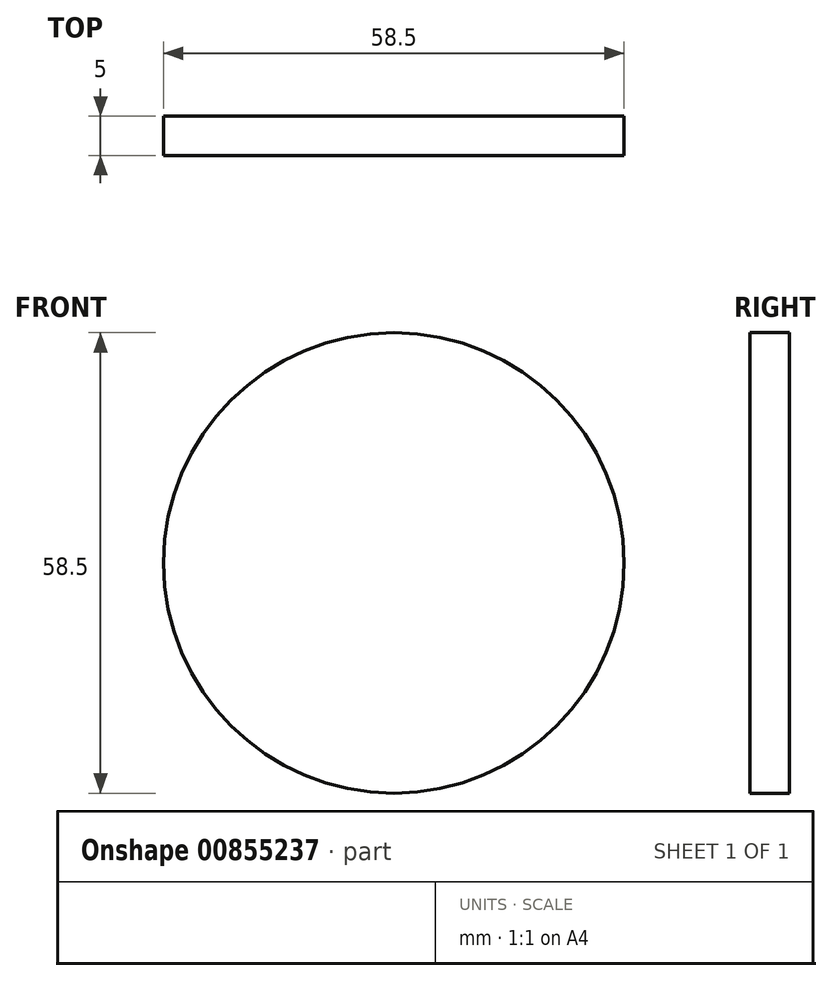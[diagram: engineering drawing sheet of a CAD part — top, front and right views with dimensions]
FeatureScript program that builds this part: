
annotation { "Feature Type Name" : "Feature", "Feature Type Description" : "" }
export const myFeature = defineFeature(function(context is Context, id is Id, definition is map)
    precondition{}
    {
        {
            var Q0;
            Q0=qCreatedBy(makeId("Front.planeOp"),FACE);
            var sketch = newSketch(context, id + "F0", { "sketchPlane" : qUnion([Q0])});
            skCircle(sketch, "E0", {"center": v(-35.75, -156.4) * mm, "radius": 29.25 * mm});
            skCircle(sketch, "E1", {"center": v(-40.8, 87.55) * mm, "radius": 24.8 * mm});
            skCircle(sketch, "E2", {"center": v(-40.8, 30.05) * mm, "radius": 24.8 * mm});
            skCircle(sketch, "E3", {"center": v(-40.8, -27.45) * mm, "radius": 24.8 * mm});
            skCircle(sketch, "E4", {"center": v(-35.75, -91.4) * mm, "radius": 29.25 * mm});
            skCircle(sketch, "E5", {"center": v(110.8, -147.35) * mm, "radius": 24.8 * mm});
            skCircle(sketch, "E6", {"center": v(110.8, -81.75) * mm, "radius": 24.8 * mm});
            skCircle(sketch, "E7", {"center": v(110.8, -16.15) * mm, "radius": 24.8 * mm});
            skCircle(sketch, "E8", {"center": v(-100.4, 87.55) * mm, "radius": 24.8 * mm});
            skCircle(sketch, "E9", {"center": v(-100.4, 30.05) * mm, "radius": 24.8 * mm});
            skCircle(sketch, "E10", {"center": v(-100.4, -27.45) * mm, "radius": 24.8 * mm});
            skCircle(sketch, "E11", {"center": v(-111.3, -91.4) * mm, "radius": 19.3 * mm});
            skCircle(sketch, "E12", {"center": v(-111.3, -145) * mm, "radius": 19.3 * mm});
            skCircle(sketch, "E13", {"center": v(-348.3, -27.45) * mm, "radius": 39.95 * mm});
            skCircle(sketch, "E14", {"center": v(-122.85, 110) * mm, "radius": 2.3 * mm});
            skCircle(sketch, "E15", {"center": v(-77.95, 65.1) * mm, "radius": 2.6 * mm});
            skArc(sketch, "E16", {"start": v(-115.72, 111.7) * mm, "mid": v(-113.34, 111.02) * mm, "end": v(-112.66, 113.4) * mm});
            skLineSegment(sketch, "E17", {"start": v(-112.66, 113.4) * mm, "end": v(-114.34, 116.45) * mm});
            skArc(sketch, "E18", {"start": v(-114.34, 116.45) * mm, "mid": v(-116.72, 117.15) * mm, "end": v(-117.41, 114.77) * mm});
            skLineSegment(sketch, "E19", {"start": v(-117.41, 114.77) * mm, "end": v(-115.72, 111.7) * mm});
            skCircle(sketch, "E20", {"center": v(-122.85, 110) * mm, "radius": 3.95 * mm});
            skCircle(sketch, "E21", {"center": v(-63.25, 110) * mm, "radius": 2.3 * mm});
            skCircle(sketch, "E22", {"center": v(-18.35, 65.1) * mm, "radius": 2.6 * mm});
            skArc(sketch, "E23", {"start": v(-56.12, 111.7) * mm, "mid": v(-53.74, 111.02) * mm, "end": v(-53.06, 113.4) * mm});
            skLineSegment(sketch, "E24", {"start": v(-53.06, 113.4) * mm, "end": v(-54.74, 116.45) * mm});
            skArc(sketch, "E25", {"start": v(-54.74, 116.45) * mm, "mid": v(-57.12, 117.15) * mm, "end": v(-57.81, 114.77) * mm});
            skLineSegment(sketch, "E26", {"start": v(-57.81, 114.77) * mm, "end": v(-56.12, 111.7) * mm});
            skCircle(sketch, "E27", {"center": v(-63.25, 110) * mm, "radius": 3.95 * mm});
            skCircle(sketch, "E28", {"center": v(-122.85, 52.5) * mm, "radius": 2.3 * mm});
            skCircle(sketch, "E29", {"center": v(-77.95, 7.6) * mm, "radius": 2.6 * mm});
            skArc(sketch, "E30", {"start": v(-115.72, 54.2) * mm, "mid": v(-113.34, 53.52) * mm, "end": v(-112.66, 55.9) * mm});
            skLineSegment(sketch, "E31", {"start": v(-112.66, 55.9) * mm, "end": v(-114.34, 58.95) * mm});
            skArc(sketch, "E32", {"start": v(-114.34, 58.95) * mm, "mid": v(-116.72, 59.65) * mm, "end": v(-117.41, 57.27) * mm});
            skLineSegment(sketch, "E33", {"start": v(-117.41, 57.27) * mm, "end": v(-115.72, 54.2) * mm});
            skCircle(sketch, "E34", {"center": v(-122.85, 52.5) * mm, "radius": 3.95 * mm});
            skCircle(sketch, "E35", {"center": v(-63.25, 52.5) * mm, "radius": 2.3 * mm});
            skCircle(sketch, "E36", {"center": v(-18.35, 7.6) * mm, "radius": 2.6 * mm});
            skArc(sketch, "E37", {"start": v(-56.12, 54.2) * mm, "mid": v(-53.74, 53.52) * mm, "end": v(-53.06, 55.9) * mm});
            skLineSegment(sketch, "E38", {"start": v(-53.06, 55.9) * mm, "end": v(-54.74, 58.95) * mm});
            skArc(sketch, "E39", {"start": v(-54.74, 58.95) * mm, "mid": v(-57.12, 59.65) * mm, "end": v(-57.81, 57.27) * mm});
            skLineSegment(sketch, "E40", {"start": v(-57.81, 57.27) * mm, "end": v(-56.12, 54.2) * mm});
            skCircle(sketch, "E41", {"center": v(-63.25, 52.5) * mm, "radius": 3.95 * mm});
            skCircle(sketch, "E42", {"center": v(-122.85, -5) * mm, "radius": 2.3 * mm});
            skCircle(sketch, "E43", {"center": v(-77.95, -49.9) * mm, "radius": 2.6 * mm});
            skArc(sketch, "E44", {"start": v(-115.72, -3.3) * mm, "mid": v(-113.34, -3.98) * mm, "end": v(-112.66, -1.6) * mm});
            skLineSegment(sketch, "E45", {"start": v(-112.66, -1.6) * mm, "end": v(-114.34, 1.45) * mm});
            skArc(sketch, "E46", {"start": v(-114.34, 1.45) * mm, "mid": v(-116.72, 2.15) * mm, "end": v(-117.41, -0.23) * mm});
            skLineSegment(sketch, "E47", {"start": v(-117.41, -0.23) * mm, "end": v(-115.72, -3.3) * mm});
            skCircle(sketch, "E48", {"center": v(-122.85, -5) * mm, "radius": 3.95 * mm});
            skCircle(sketch, "E49", {"center": v(-63.25, -5) * mm, "radius": 2.3 * mm});
            skCircle(sketch, "E50", {"center": v(-18.35, -49.9) * mm, "radius": 2.6 * mm});
            skArc(sketch, "E51", {"start": v(-56.12, -3.3) * mm, "mid": v(-53.74, -3.98) * mm, "end": v(-53.06, -1.6) * mm});
            skLineSegment(sketch, "E52", {"start": v(-53.06, -1.6) * mm, "end": v(-54.74, 1.45) * mm});
            skArc(sketch, "E53", {"start": v(-54.74, 1.45) * mm, "mid": v(-57.12, 2.15) * mm, "end": v(-57.81, -0.23) * mm});
            skLineSegment(sketch, "E54", {"start": v(-57.81, -0.23) * mm, "end": v(-56.12, -3.3) * mm});
            skCircle(sketch, "E55", {"center": v(-63.25, -5) * mm, "radius": 3.95 * mm});
            skCircle(sketch, "E56", {"center": v(88.35, 6.3) * mm, "radius": 2.3 * mm});
            skCircle(sketch, "E57", {"center": v(133.25, -38.6) * mm, "radius": 2.6 * mm});
            skArc(sketch, "E58", {"start": v(95.48, 8) * mm, "mid": v(97.86, 7.32) * mm, "end": v(98.54, 9.7) * mm});
            skLineSegment(sketch, "E59", {"start": v(98.54, 9.7) * mm, "end": v(96.86, 12.75) * mm});
            skArc(sketch, "E60", {"start": v(96.86, 12.75) * mm, "mid": v(94.48, 13.45) * mm, "end": v(93.79, 11.07) * mm});
            skLineSegment(sketch, "E61", {"start": v(93.79, 11.07) * mm, "end": v(95.48, 8) * mm});
            skCircle(sketch, "E62", {"center": v(88.35, 6.3) * mm, "radius": 3.95 * mm});
            skCircle(sketch, "E63", {"center": v(88.35, -59.3) * mm, "radius": 2.3 * mm});
            skCircle(sketch, "E64", {"center": v(133.25, -104.2) * mm, "radius": 2.6 * mm});
            skArc(sketch, "E65", {"start": v(95.48, -57.6) * mm, "mid": v(97.86, -58.28) * mm, "end": v(98.54, -55.9) * mm});
            skLineSegment(sketch, "E66", {"start": v(98.54, -55.9) * mm, "end": v(96.86, -52.85) * mm});
            skArc(sketch, "E67", {"start": v(96.86, -52.85) * mm, "mid": v(94.48, -52.15) * mm, "end": v(93.79, -54.53) * mm});
            skLineSegment(sketch, "E68", {"start": v(93.79, -54.53) * mm, "end": v(95.48, -57.6) * mm});
            skCircle(sketch, "E69", {"center": v(88.35, -59.3) * mm, "radius": 3.95 * mm});
            skCircle(sketch, "E70", {"center": v(88.35, -124.9) * mm, "radius": 2.3 * mm});
            skCircle(sketch, "E71", {"center": v(133.25, -169.8) * mm, "radius": 2.6 * mm});
            skArc(sketch, "E72", {"start": v(95.48, -123.2) * mm, "mid": v(97.86, -123.88) * mm, "end": v(98.54, -121.5) * mm});
            skLineSegment(sketch, "E73", {"start": v(98.54, -121.5) * mm, "end": v(96.86, -118.45) * mm});
            skArc(sketch, "E74", {"start": v(96.86, -118.45) * mm, "mid": v(94.48, -117.75) * mm, "end": v(93.79, -120.13) * mm});
            skLineSegment(sketch, "E75", {"start": v(93.79, -120.13) * mm, "end": v(95.48, -123.2) * mm});
            skCircle(sketch, "E76", {"center": v(88.35, -124.9) * mm, "radius": 3.95 * mm});
            skCircle(sketch, "E77", {"center": v(-94.72, -74.82) * mm, "radius": 1.5 * mm});
            skCircle(sketch, "E78", {"center": v(-94.72, -107.98) * mm, "radius": 1.5 * mm});
            skCircle(sketch, "E79", {"center": v(-127.88, -74.82) * mm, "radius": 1.5 * mm});
            skCircle(sketch, "E80", {"center": v(-127.88, -107.98) * mm, "radius": 1.5 * mm});
            skCircle(sketch, "E81", {"center": v(-94.72, -128.42) * mm, "radius": 1.5 * mm});
            skCircle(sketch, "E82", {"center": v(-94.72, -161.58) * mm, "radius": 1.5 * mm});
            skCircle(sketch, "E83", {"center": v(-127.88, -128.42) * mm, "radius": 1.5 * mm});
            skCircle(sketch, "E84", {"center": v(-127.88, -161.58) * mm, "radius": 1.5 * mm});
            skCircle(sketch, "E85", {"center": v(-59.3, -132.85) * mm, "radius": 1.5 * mm});
            skCircle(sketch, "E86", {"center": v(-12.2, -132.85) * mm, "radius": 1.5 * mm});
            skCircle(sketch, "E87", {"center": v(-59.3, -179.95) * mm, "radius": 1.5 * mm});
            skCircle(sketch, "E88", {"center": v(-12.2, -179.95) * mm, "radius": 1.5 * mm});
            skCircle(sketch, "E89", {"center": v(-59.3, -67.85) * mm, "radius": 1.5 * mm});
            skCircle(sketch, "E90", {"center": v(-12.2, -67.85) * mm, "radius": 1.5 * mm});
            skCircle(sketch, "E91", {"center": v(-59.3, -114.95) * mm, "radius": 1.5 * mm});
            skCircle(sketch, "E92", {"center": v(-12.2, -114.95) * mm, "radius": 1.5 * mm});
            skCircle(sketch, "E93", {"center": v(212.15, 64.6) * mm, "radius": 40.1 * mm});
            skCircle(sketch, "E94", {"center": v(-444.4, 72.45) * mm, "radius": 40.1 * mm});
            skLineSegment(sketch, "E95", {"start": v(-395.3, 22.5) * mm, "end": v(-395.3, 130.5) * mm});
            skLineSegment(sketch, "E96", {"start": v(-395.3, 130.5) * mm, "end": v(-301.3, 130.5) * mm});
            skLineSegment(sketch, "E97", {"start": v(-301.3, 130.5) * mm, "end": v(-301.3, 22.5) * mm});
            skLineSegment(sketch, "E98", {"start": v(-301.3, 22.5) * mm, "end": v(-395.3, 22.5) * mm});
            skCircle(sketch, "E99", {"center": v(110.95, 64.6) * mm, "radius": 40.1 * mm});
            skCircle(sketch, "E100", {"center": v(211.85, -139.55) * mm, "radius": 40.1 * mm});
            skCircle(sketch, "E101", {"center": v(79.52, 96.03) * mm, "radius": 2.3 * mm});
            skCircle(sketch, "E102", {"center": v(79.52, 96.03) * mm, "radius": 3.95 * mm});
            skCircle(sketch, "E103", {"center": v(142.38, 33.17) * mm, "radius": 2.6 * mm});
            skArc(sketch, "E104", {"start": v(85.3, 100.02) * mm, "mid": v(87.72, 99.53) * mm, "end": v(88.2, 101.96) * mm});
            skLineSegment(sketch, "E105", {"start": v(88.2, 101.96) * mm, "end": v(86.28, 104.86) * mm});
            skArc(sketch, "E106", {"start": v(86.28, 104.86) * mm, "mid": v(83.85, 105.37) * mm, "end": v(83.36, 102.94) * mm});
            skLineSegment(sketch, "E107", {"start": v(83.36, 102.94) * mm, "end": v(85.3, 100.02) * mm});
            skArc(sketch, "E108", {"start": v(136.6, 100.02) * mm, "mid": v(134.18, 99.53) * mm, "end": v(133.7, 101.96) * mm});
            skLineSegment(sketch, "E109", {"start": v(133.7, 101.96) * mm, "end": v(135.62, 104.86) * mm});
            skArc(sketch, "E110", {"start": v(135.62, 104.86) * mm, "mid": v(138.05, 105.37) * mm, "end": v(138.54, 102.94) * mm});
            skLineSegment(sketch, "E111", {"start": v(138.54, 102.94) * mm, "end": v(136.6, 100.02) * mm});
            skCircle(sketch, "E112", {"center": v(180.42, -108.12) * mm, "radius": 1.5 * mm});
            skCircle(sketch, "E113", {"center": v(243.28, -108.12) * mm, "radius": 1.5 * mm});
            skCircle(sketch, "E114", {"center": v(243.28, -170.98) * mm, "radius": 1.5 * mm});
            skCircle(sketch, "E115", {"center": v(180.42, -170.98) * mm, "radius": 1.5 * mm});
            skCircle(sketch, "E116", {"center": v(180.72, 96.03) * mm, "radius": 1.5 * mm});
            skCircle(sketch, "E117", {"center": v(243.58, 96.03) * mm, "radius": 1.5 * mm});
            skCircle(sketch, "E118", {"center": v(243.58, 33.17) * mm, "radius": 1.5 * mm});
            skCircle(sketch, "E119", {"center": v(180.72, 33.17) * mm, "radius": 1.5 * mm});
            skCircle(sketch, "E120", {"center": v(-379.73, 3.98) * mm, "radius": 1.5 * mm});
            skCircle(sketch, "E121", {"center": v(-316.87, 3.98) * mm, "radius": 1.5 * mm});
            skCircle(sketch, "E122", {"center": v(-316.87, -58.88) * mm, "radius": 1.5 * mm});
            skCircle(sketch, "E123", {"center": v(-379.73, -58.88) * mm, "radius": 1.5 * mm});
            skCircle(sketch, "E124", {"center": v(-475.83, 103.88) * mm, "radius": 1.5 * mm});
            skCircle(sketch, "E125", {"center": v(-412.97, 103.88) * mm, "radius": 1.5 * mm});
            skCircle(sketch, "E126", {"center": v(-412.97, 41.02) * mm, "radius": 1.5 * mm});
            skCircle(sketch, "E127", {"center": v(-475.83, 41.02) * mm, "radius": 1.5 * mm});
            skCircle(sketch, "E128", {"center": v(294.67, -108.12) * mm, "radius": 1.5 * mm});
            skCircle(sketch, "E129", {"center": v(357.53, -108.12) * mm, "radius": 1.5 * mm});
            skCircle(sketch, "E130", {"center": v(357.53, -170.98) * mm, "radius": 1.5 * mm});
            skLineSegment(sketch, "E131", {"start": v(315.8, -180.65) * mm, "end": v(299.2, -180.65) * mm});
            skArc(sketch, "E132", {"start": v(299.2, -180.65) * mm, "mid": v(289.16, -176.49) * mm, "end": v(285, -166.45) * mm});
            skLineSegment(sketch, "E133", {"start": v(285, -166.45) * mm, "end": v(285, -150.65) * mm});
            skArc(sketch, "E134", {"start": v(285, -150.65) * mm, "mid": v(285.14, -149.92) * mm, "end": v(285.52, -149.3) * mm});
            skArc(sketch, "E135", {"start": v(285.52, -149.3) * mm, "mid": v(286.4, -147.75) * mm, "end": v(286.52, -145.96) * mm});
            skArc(sketch, "E136", {"start": v(286.52, -145.96) * mm, "mid": v(354.23, -110.97) * mm, "end": v(320.3, -179.23) * mm});
            skArc(sketch, "E137", {"start": v(320.3, -179.23) * mm, "mid": v(318.6, -179.34) * mm, "end": v(317.1, -180.16) * mm});
            skArc(sketch, "E138", {"start": v(317.1, -180.16) * mm, "mid": v(316.5, -180.52) * mm, "end": v(315.8, -180.65) * mm});
            skCircle(sketch, "E139", {"center": v(-287.13, 103.88) * mm, "radius": 1.5 * mm});
            skCircle(sketch, "E140", {"center": v(-224.27, 103.88) * mm, "radius": 1.5 * mm});
            skCircle(sketch, "E141", {"center": v(-224.27, 41.02) * mm, "radius": 1.5 * mm});
            skLineSegment(sketch, "E142", {"start": v(-266, 31.35) * mm, "end": v(-282.6, 31.35) * mm});
            skArc(sketch, "E143", {"start": v(-282.6, 31.35) * mm, "mid": v(-292.64, 35.51) * mm, "end": v(-296.8, 45.55) * mm});
            skLineSegment(sketch, "E144", {"start": v(-296.8, 45.55) * mm, "end": v(-296.8, 61.35) * mm});
            skArc(sketch, "E145", {"start": v(-296.8, 61.35) * mm, "mid": v(-296.66, 62.08) * mm, "end": v(-296.28, 62.7) * mm});
            skArc(sketch, "E146", {"start": v(-296.28, 62.7) * mm, "mid": v(-295.4, 64.25) * mm, "end": v(-295.28, 66.04) * mm});
            skArc(sketch, "E147", {"start": v(-295.28, 66.04) * mm, "mid": v(-227.57, 101.03) * mm, "end": v(-261.5, 32.77) * mm});
            skArc(sketch, "E148", {"start": v(-261.5, 32.77) * mm, "mid": v(-263.2, 32.66) * mm, "end": v(-264.7, 31.84) * mm});
            skArc(sketch, "E149", {"start": v(-264.7, 31.84) * mm, "mid": v(-265.3, 31.48) * mm, "end": v(-266, 31.35) * mm});
            skCircle(sketch, "E150", {"center": v(-287.13, 3.98) * mm, "radius": 1.5 * mm});
            skCircle(sketch, "E151", {"center": v(-224.27, 3.98) * mm, "radius": 1.5 * mm});
            skCircle(sketch, "E152", {"center": v(-224.27, -58.88) * mm, "radius": 1.5 * mm});
            skLineSegment(sketch, "E153", {"start": v(-266, -68.55) * mm, "end": v(-282.6, -68.55) * mm});
            skArc(sketch, "E154", {"start": v(-282.6, -68.55) * mm, "mid": v(-292.64, -64.39) * mm, "end": v(-296.8, -54.35) * mm});
            skLineSegment(sketch, "E155", {"start": v(-296.8, -54.35) * mm, "end": v(-296.8, -38.55) * mm});
            skArc(sketch, "E156", {"start": v(-296.8, -38.55) * mm, "mid": v(-296.66, -37.82) * mm, "end": v(-296.28, -37.2) * mm});
            skArc(sketch, "E157", {"start": v(-296.28, -37.2) * mm, "mid": v(-295.4, -35.65) * mm, "end": v(-295.28, -33.86) * mm});
            skArc(sketch, "E158", {"start": v(-295.28, -33.86) * mm, "mid": v(-227.57, 1.13) * mm, "end": v(-261.5, -67.13) * mm});
            skArc(sketch, "E159", {"start": v(-261.5, -67.13) * mm, "mid": v(-263.2, -67.24) * mm, "end": v(-264.7, -68.06) * mm});
            skArc(sketch, "E160", {"start": v(-264.7, -68.06) * mm, "mid": v(-265.3, -68.42) * mm, "end": v(-266, -68.55) * mm});
            skCircle(sketch, "E161", {"center": v(407.67, 3.98) * mm, "radius": 1.5 * mm});
            skCircle(sketch, "E162", {"center": v(470.53, 3.98) * mm, "radius": 1.5 * mm});
            skCircle(sketch, "E163", {"center": v(470.53, -58.88) * mm, "radius": 1.5 * mm});
            skLineSegment(sketch, "E164", {"start": v(428.8, -68.55) * mm, "end": v(412.2, -68.55) * mm});
            skArc(sketch, "E165", {"start": v(412.2, -68.55) * mm, "mid": v(402.16, -64.39) * mm, "end": v(398, -54.35) * mm});
            skLineSegment(sketch, "E166", {"start": v(398, -54.35) * mm, "end": v(398, -38.55) * mm});
            skArc(sketch, "E167", {"start": v(398, -38.55) * mm, "mid": v(398.14, -37.82) * mm, "end": v(398.52, -37.2) * mm});
            skArc(sketch, "E168", {"start": v(398.52, -37.2) * mm, "mid": v(399.4, -35.65) * mm, "end": v(399.52, -33.86) * mm});
            skArc(sketch, "E169", {"start": v(399.52, -33.86) * mm, "mid": v(467.23, 1.13) * mm, "end": v(433.3, -67.13) * mm});
            skArc(sketch, "E170", {"start": v(433.3, -67.13) * mm, "mid": v(431.6, -67.24) * mm, "end": v(430.1, -68.06) * mm});
            skArc(sketch, "E171", {"start": v(430.1, -68.06) * mm, "mid": v(429.5, -68.42) * mm, "end": v(428.8, -68.55) * mm});
            skCircle(sketch, "E172", {"center": v(407.67, 103.88) * mm, "radius": 1.5 * mm});
            skCircle(sketch, "E173", {"center": v(470.53, 103.88) * mm, "radius": 1.5 * mm});
            skCircle(sketch, "E174", {"center": v(470.53, 41.02) * mm, "radius": 1.5 * mm});
            skLineSegment(sketch, "E175", {"start": v(428.8, 31.35) * mm, "end": v(412.2, 31.35) * mm});
            skArc(sketch, "E176", {"start": v(412.2, 31.35) * mm, "mid": v(402.16, 35.51) * mm, "end": v(398, 45.55) * mm});
            skLineSegment(sketch, "E177", {"start": v(398, 45.55) * mm, "end": v(398, 61.35) * mm});
            skArc(sketch, "E178", {"start": v(398, 61.35) * mm, "mid": v(398.14, 62.08) * mm, "end": v(398.52, 62.7) * mm});
            skArc(sketch, "E179", {"start": v(398.52, 62.7) * mm, "mid": v(399.4, 64.25) * mm, "end": v(399.52, 66.04) * mm});
            skArc(sketch, "E180", {"start": v(399.52, 66.04) * mm, "mid": v(467.23, 101.03) * mm, "end": v(433.3, 32.77) * mm});
            skArc(sketch, "E181", {"start": v(433.3, 32.77) * mm, "mid": v(431.6, 32.66) * mm, "end": v(430.1, 31.84) * mm});
            skArc(sketch, "E182", {"start": v(430.1, 31.84) * mm, "mid": v(429.5, 31.48) * mm, "end": v(428.8, 31.35) * mm});
            skCircle(sketch, "E183", {"center": v(383.35, 5.05) * mm, "radius": 1.8 * mm});
            skCircle(sketch, "E184", {"center": v(269.15, 5.05) * mm, "radius": 1.8 * mm});
            skCircle(sketch, "E185", {"center": v(383.35, 125.65) * mm, "radius": 1.8 * mm});
            skCircle(sketch, "E186", {"center": v(269.15, 125.65) * mm, "radius": 1.8 * mm});
            skArc(sketch, "E187", {"start": v(263.84, 16.77) * mm, "mid": v(263.4, 17.42) * mm, "end": v(263.25, 18.18) * mm});
            skLineSegment(sketch, "E188", {"start": v(263.25, 18.18) * mm, "end": v(263.25, 112.52) * mm});
            skArc(sketch, "E189", {"start": v(263.25, 112.52) * mm, "mid": v(263.4, 113.29) * mm, "end": v(263.84, 113.94) * mm});
            skLineSegment(sketch, "E190", {"start": v(263.84, 113.94) * mm, "end": v(280.66, 130.77) * mm});
            skArc(sketch, "E191", {"start": v(280.66, 130.77) * mm, "mid": v(281.31, 131.2) * mm, "end": v(282.08, 131.35) * mm});
            skLineSegment(sketch, "E192", {"start": v(282.08, 131.35) * mm, "end": v(370.42, 131.35) * mm});
            skArc(sketch, "E193", {"start": v(370.42, 131.35) * mm, "mid": v(371.19, 131.2) * mm, "end": v(371.84, 130.77) * mm});
            skLineSegment(sketch, "E194", {"start": v(371.84, 130.77) * mm, "end": v(388.66, 113.94) * mm});
            skArc(sketch, "E195", {"start": v(388.66, 113.94) * mm, "mid": v(389.1, 113.29) * mm, "end": v(389.25, 112.52) * mm});
            skLineSegment(sketch, "E196", {"start": v(389.25, 112.52) * mm, "end": v(389.25, 18.18) * mm});
            skArc(sketch, "E197", {"start": v(389.25, 18.18) * mm, "mid": v(389.1, 17.42) * mm, "end": v(388.66, 16.77) * mm});
            skLineSegment(sketch, "E198", {"start": v(388.66, 16.77) * mm, "end": v(371.84, -0.06) * mm});
            skArc(sketch, "E199", {"start": v(371.84, -0.06) * mm, "mid": v(371.19, -0.5) * mm, "end": v(370.42, -0.65) * mm});
            skLineSegment(sketch, "E200", {"start": v(370.42, -0.65) * mm, "end": v(282.08, -0.65) * mm});
            skArc(sketch, "E201", {"start": v(282.08, -0.65) * mm, "mid": v(281.31, -0.5) * mm, "end": v(280.66, -0.06) * mm});
            skLineSegment(sketch, "E202", {"start": v(280.66, -0.06) * mm, "end": v(263.84, 16.77) * mm});
            skCircle(sketch, "E203", {"center": v(288, -11.44) * mm, "radius": 1.5 * mm});
            skCircle(sketch, "E204", {"center": v(364.2, -11.44) * mm, "radius": 1.5 * mm});
            skCircle(sketch, "E205", {"center": v(364.2, -87.64) * mm, "radius": 1.5 * mm});
            skCircle(sketch, "E206", {"center": v(288, -87.64) * mm, "radius": 1.5 * mm});
            skLineSegment(sketch, "E207", {"start": v(296, -8.65) * mm, "end": v(285.2, -19.46) * mm});
            skLineSegment(sketch, "E208", {"start": v(285.2, -19.46) * mm, "end": v(285.2, -79.65) * mm});
            skLineSegment(sketch, "E209", {"start": v(285.2, -79.65) * mm, "end": v(296, -90.45) * mm});
            skLineSegment(sketch, "E210", {"start": v(296, -90.45) * mm, "end": v(356.2, -90.45) * mm});
            skLineSegment(sketch, "E211", {"start": v(356.2, -90.45) * mm, "end": v(367, -79.64) * mm});
            skLineSegment(sketch, "E212", {"start": v(367, -79.64) * mm, "end": v(367, -19.45) * mm});
            skLineSegment(sketch, "E213", {"start": v(367, -19.45) * mm, "end": v(356.19, -8.65) * mm});
            skLineSegment(sketch, "E214", {"start": v(356.19, -8.65) * mm, "end": v(296, -8.65) * mm});
            skArc(sketch, "E215", {"start": v(-119.73, -120.84) * mm, "mid": v(-117.58, -122.07) * mm, "end": v(-116.35, -119.92) * mm});
            skLineSegment(sketch, "E216", {"start": v(-116.35, -119.92) * mm, "end": v(-117.27, -116.56) * mm});
            skArc(sketch, "E217", {"start": v(-117.27, -116.56) * mm, "mid": v(-119.42, -115.32) * mm, "end": v(-120.65, -117.47) * mm});
            skLineSegment(sketch, "E218", {"start": v(-120.65, -117.47) * mm, "end": v(-119.73, -120.84) * mm});
            skArc(sketch, "E219", {"start": v(-119.73, -67.24) * mm, "mid": v(-117.58, -68.47) * mm, "end": v(-116.35, -66.32) * mm});
            skLineSegment(sketch, "E220", {"start": v(-116.35, -66.32) * mm, "end": v(-117.27, -62.96) * mm});
            skArc(sketch, "E221", {"start": v(-117.27, -62.96) * mm, "mid": v(-119.42, -61.72) * mm, "end": v(-120.65, -63.87) * mm});
            skLineSegment(sketch, "E222", {"start": v(-120.65, -63.87) * mm, "end": v(-119.73, -67.24) * mm});
            skCircle(sketch, "E223", {"center": v(60.5, -185.65) * mm, "radius": 2.5 * mm});
            skCircle(sketch, "E224", {"center": v(87, -185.65) * mm, "radius": 2.5 * mm});
            skCircle(sketch, "E225", {"center": v(109, -188.65) * mm, "radius": 2.5 * mm});
            skCircle(sketch, "E226", {"center": v(180, -188.65) * mm, "radius": 2.5 * mm});
            skCircle(sketch, "E227", {"center": v(255, -185.65) * mm, "radius": 2.5 * mm});
            skCircle(sketch, "E228", {"center": v(54, -135.15) * mm, "radius": 2.5 * mm});
            skCircle(sketch, "E229", {"center": v(161.5, -138.65) * mm, "radius": 2.5 * mm});
            skCircle(sketch, "E230", {"center": v(158, -112.65) * mm, "radius": 2.5 * mm});
            skCircle(sketch, "E231", {"center": v(275, -138.65) * mm, "radius": 2.5 * mm});
            skCircle(sketch, "E232", {"center": v(270, -92.65) * mm, "radius": 2.5 * mm});
            skCircle(sketch, "E233", {"center": v(451, -83.65) * mm, "radius": 2.5 * mm});
            skCircle(sketch, "E234", {"center": v(276.5, -50.65) * mm, "radius": 2.5 * mm});
            skCircle(sketch, "E235", {"center": v(376.5, 142.68) * mm, "radius": 2.5 * mm});
            skCircle(sketch, "E236", {"center": v(193, 179.39) * mm, "radius": 2.5 * mm});
            skCircle(sketch, "E237", {"center": v(-6, 147.35) * mm, "radius": 2.5 * mm});
            skCircle(sketch, "E238", {"center": v(5.5, 187.49) * mm, "radius": 2.5 * mm});
            skCircle(sketch, "E239", {"center": v(25.5, 147.35) * mm, "radius": 2.5 * mm});
            skCircle(sketch, "E240", {"center": v(494, 69.35) * mm, "radius": 2.5 * mm});
            skCircle(sketch, "E241", {"center": v(494, 31.35) * mm, "radius": 2.5 * mm});
            skCircle(sketch, "E242", {"center": v(494, 6.35) * mm, "radius": 2.5 * mm});
            skCircle(sketch, "E243", {"center": v(494, -26.65) * mm, "radius": 2.5 * mm});
            skCircle(sketch, "E244", {"center": v(494, -59.65) * mm, "radius": 2.5 * mm});
            skCircle(sketch, "E245", {"center": v(495, -144.65) * mm, "radius": 2.5 * mm});
            skCircle(sketch, "E246", {"center": v(-437, 16.35) * mm, "radius": 2.5 * mm});
            skCircle(sketch, "E247", {"center": v(-494, 81.35) * mm, "radius": 2.5 * mm});
            skCircle(sketch, "E248", {"center": v(-494, -17.15) * mm, "radius": 2.5 * mm});
            skCircle(sketch, "E249", {"center": v(-494, -128.65) * mm, "radius": 2.5 * mm});
            skCircle(sketch, "E250", {"center": v(-370, 157.67) * mm, "radius": 2.5 * mm});
            skCircle(sketch, "E251", {"center": v(-183.5, 184.34) * mm, "radius": 2.5 * mm});
            skCircle(sketch, "E252", {"center": v(-443, -166.65) * mm, "radius": 2.5 * mm});
            skCircle(sketch, "E253", {"center": v(-389, -174.65) * mm, "radius": 2.5 * mm});
            skCircle(sketch, "E254", {"center": v(-317.5, -190.15) * mm, "radius": 2.5 * mm});
            skCircle(sketch, "E255", {"center": v(-263.5, -186.65) * mm, "radius": 2.5 * mm});
            skCircle(sketch, "E256", {"center": v(-295, -186.65) * mm, "radius": 2.5 * mm});
            skCircle(sketch, "E257", {"center": v(-233.5, 147.35) * mm, "radius": 2.5 * mm});
            skCircle(sketch, "E258", {"center": v(-202, 147.35) * mm, "radius": 2.5 * mm});
            skCircle(sketch, "E259", {"center": v(-116.5, 150.35) * mm, "radius": 2.5 * mm});
            skCircle(sketch, "E260", {"center": v(-202, -5.15) * mm, "radius": 2.5 * mm});
            skCircle(sketch, "E261", {"center": v(-300.5, -25.65) * mm, "radius": 2.5 * mm});
            skCircle(sketch, "E262", {"center": v(-387.3, 137) * mm, "radius": 1.5 * mm});
            skCircle(sketch, "E263", {"center": v(-348.3, 137) * mm, "radius": 1.5 * mm});
            skCircle(sketch, "E264", {"center": v(-309.3, 137) * mm, "radius": 1.5 * mm});
            skCircle(sketch, "E265", {"center": v(-387.3, 17) * mm, "radius": 1.5 * mm});
            skCircle(sketch, "E266", {"center": v(-309.3, 17) * mm, "radius": 1.5 * mm});
            skArc(sketch, "E267", {"start": v(444.02, -145.44) * mm, "mid": v(441.5, -145.35) * mm, "end": v(439.27, -146.5) * mm});
            skArc(sketch, "E268", {"start": v(439.27, -146.5) * mm, "mid": v(423.78, -146) * mm, "end": v(423.48, -130.5) * mm});
            skArc(sketch, "E269", {"start": v(423.48, -130.5) * mm, "mid": v(424.66, -128.28) * mm, "end": v(424.6, -125.77) * mm});
            skArc(sketch, "E270", {"start": v(424.6, -125.77) * mm, "mid": v(432.05, -97.44) * mm, "end": v(460.48, -90.35) * mm});
            skArc(sketch, "E271", {"start": v(460.48, -90.35) * mm, "mid": v(463, -90.44) * mm, "end": v(465.23, -89.3) * mm});
            skArc(sketch, "E272", {"start": v(465.23, -89.3) * mm, "mid": v(480.72, -89.8) * mm, "end": v(481.02, -105.29) * mm});
            skArc(sketch, "E273", {"start": v(481.02, -105.29) * mm, "mid": v(479.84, -107.51) * mm, "end": v(479.9, -110.03) * mm});
            skArc(sketch, "E274", {"start": v(479.9, -110.03) * mm, "mid": v(472.45, -138.36) * mm, "end": v(444.02, -145.44) * mm});
            skCircle(sketch, "E275", {"center": v(428.5, -94.15) * mm, "radius": 1.5 * mm});
            skCircle(sketch, "E276", {"center": v(476, -141.65) * mm, "radius": 1.5 * mm});
            skCircle(sketch, "E277", {"center": v(487.5, -130.15) * mm, "radius": 2.5 * mm});
            skArc(sketch, "E278", {"start": v(129.49, 191.52) * mm, "mid": v(-17.73, 194.63) * mm, "end": v(-164.95, 192.46) * mm});
            skLineSegment(sketch, "E279", {"start": v(-164.95, 192.46) * mm, "end": v(-191.07, 190.89) * mm});
            skArc(sketch, "E280", {"start": v(-191.07, 190.89) * mm, "mid": v(-200, 190.29) * mm, "end": v(-208.91, 189.55) * mm});
            skLineSegment(sketch, "E281", {"start": v(-208.91, 189.55) * mm, "end": v(-232.33, 187.44) * mm});
            skArc(sketch, "E282", {"start": v(-232.33, 187.44) * mm, "mid": v(-249.97, 185.6) * mm, "end": v(-267.55, 183.22) * mm});
            skLineSegment(sketch, "E283", {"start": v(-267.55, 183.22) * mm, "end": v(-288.6, 180.06) * mm});
            skArc(sketch, "E284", {"start": v(-288.6, 180.06) * mm, "mid": v(-299.98, 178.24) * mm, "end": v(-311.32, 176.2) * mm});
            skLineSegment(sketch, "E285", {"start": v(-311.32, 176.2) * mm, "end": v(-344.06, 170) * mm});
            skArc(sketch, "E286", {"start": v(-344.06, 170) * mm, "mid": v(-350, 168.85) * mm, "end": v(-355.92, 167.63) * mm});
            skLineSegment(sketch, "E287", {"start": v(-355.92, 167.63) * mm, "end": v(-380.75, 162.4) * mm});
            skArc(sketch, "E288", {"start": v(-380.75, 162.4) * mm, "mid": v(-399.92, 158.04) * mm, "end": v(-418.94, 153.05) * mm});
            skLineSegment(sketch, "E289", {"start": v(-418.94, 153.05) * mm, "end": v(-436.76, 148.06) * mm});
            skArc(sketch, "E290", {"start": v(-436.76, 148.06) * mm, "mid": v(-449.95, 144.2) * mm, "end": v(-463.05, 140.04) * mm});
            skLineSegment(sketch, "E291", {"start": v(-463.05, 140.04) * mm, "end": v(-492.34, 130.38) * mm});
            skArc(sketch, "E292", {"start": v(-492.34, 130.38) * mm, "mid": v(-499.7, 124.9) * mm, "end": v(-502.5, 116.18) * mm});
            skLineSegment(sketch, "E293", {"start": v(-502.5, 116.18) * mm, "end": v(-502.5, -130.65) * mm});
            skArc(sketch, "E294", {"start": v(-502.5, -130.65) * mm, "mid": v(-487.86, -166) * mm, "end": v(-452.5, -180.65) * mm});
            skLineSegment(sketch, "E295", {"start": v(-452.5, -180.65) * mm, "end": v(-375.8, -180.65) * mm});
            skArc(sketch, "E296", {"start": v(-375.8, -180.65) * mm, "mid": v(-367.61, -181.32) * mm, "end": v(-359.64, -183.33) * mm});
            skLineSegment(sketch, "E297", {"start": v(-359.64, -183.33) * mm, "end": v(-334.36, -191.97) * mm});
            skArc(sketch, "E298", {"start": v(-334.36, -191.97) * mm, "mid": v(-326.39, -193.97) * mm, "end": v(-318.2, -194.65) * mm});
            skLineSegment(sketch, "E299", {"start": v(-318.2, -194.65) * mm, "end": v(452.5, -194.65) * mm});
            skArc(sketch, "E300", {"start": v(452.5, -194.65) * mm, "mid": v(487.86, -180) * mm, "end": v(502.5, -144.65) * mm});
            skLineSegment(sketch, "E301", {"start": v(502.5, -144.65) * mm, "end": v(502.5, 97.16) * mm});
            skArc(sketch, "E302", {"start": v(502.5, 97.16) * mm, "mid": v(499.9, 105.61) * mm, "end": v(492.98, 111.13) * mm});
            skLineSegment(sketch, "E303", {"start": v(492.98, 111.13) * mm, "end": v(469.73, 120.17) * mm});
            skArc(sketch, "E304", {"start": v(469.73, 120.17) * mm, "mid": v(449.88, 127.5) * mm, "end": v(429.78, 134.12) * mm});
            skLineSegment(sketch, "E305", {"start": v(429.78, 134.12) * mm, "end": v(410.57, 140.07) * mm});
            skArc(sketch, "E306", {"start": v(410.57, 140.07) * mm, "mid": v(399.97, 143.25) * mm, "end": v(389.31, 146.24) * mm});
            skLineSegment(sketch, "E307", {"start": v(389.31, 146.24) * mm, "end": v(360.9, 153.9) * mm});
            skArc(sketch, "E308", {"start": v(360.9, 153.9) * mm, "mid": v(349.97, 156.75) * mm, "end": v(339, 159.38) * mm});
            skLineSegment(sketch, "E309", {"start": v(339, 159.38) * mm, "end": v(308.38, 166.42) * mm});
            skArc(sketch, "E310", {"start": v(308.38, 166.42) * mm, "mid": v(299.99, 168.3) * mm, "end": v(291.56, 170.04) * mm});
            skLineSegment(sketch, "E311", {"start": v(291.56, 170.04) * mm, "end": v(264.27, 175.5) * mm});
            skArc(sketch, "E312", {"start": v(264.27, 175.5) * mm, "mid": v(249.97, 178.18) * mm, "end": v(235.6, 180.51) * mm});
            skLineSegment(sketch, "E313", {"start": v(235.6, 180.51) * mm, "end": v(217.55, 183.22) * mm});
            skArc(sketch, "E314", {"start": v(217.55, 183.22) * mm, "mid": v(199.97, 185.6) * mm, "end": v(182.33, 187.44) * mm});
            skLineSegment(sketch, "E315", {"start": v(182.33, 187.44) * mm, "end": v(158.91, 189.55) * mm});
            skArc(sketch, "E316", {"start": v(158.91, 189.55) * mm, "mid": v(150, 190.29) * mm, "end": v(141.07, 190.89) * mm});
            skLineSegment(sketch, "E317", {"start": v(141.07, 190.89) * mm, "end": v(135.74, 191.2) * mm});
            skArc(sketch, "E318", {"start": v(135.74, 191.2) * mm, "mid": v(132.61, 191.38) * mm, "end": v(129.49, 191.52) * mm});
            skCircle(sketch, "E319", {"center": v(16.5, -156.15) * mm, "radius": 6.5 * mm});
            skCircle(sketch, "E320", {"center": v(16.5, -146.65) * mm, "radius": 2 * mm});
            skCircle(sketch, "E321", {"center": v(29.5, 87.35) * mm, "radius": 6.5 * mm});
            skCircle(sketch, "E322", {"center": v(451, -169.65) * mm, "radius": 7 * mm});
            skCircle(sketch, "E323", {"center": v(394.5, -157.65) * mm, "radius": 5.5 * mm});
            skCircle(sketch, "E324", {"center": v(394.5, -120.15) * mm, "radius": 6 * mm});
            skCircle(sketch, "E325", {"center": v(394.5, -92.15) * mm, "radius": 6 * mm});
            skCircle(sketch, "E326", {"center": v(67.5, 151.85) * mm, "radius": 8 * mm});
            skCircle(sketch, "E327", {"center": v(85, 151.85) * mm, "radius": 8 * mm});
            skCircle(sketch, "E328", {"center": v(140.5, 151.35) * mm, "radius": 9 * mm});
            skLineSegment(sketch, "E329", {"start": v(173, 157.35) * mm, "end": v(207, 157.35) * mm});
            skLineSegment(sketch, "E330", {"start": v(207, 157.35) * mm, "end": v(207, 143.35) * mm});
            skLineSegment(sketch, "E331", {"start": v(207, 143.35) * mm, "end": v(173, 143.35) * mm});
            skLineSegment(sketch, "E332", {"start": v(173, 143.35) * mm, "end": v(173, 157.35) * mm});
            skCircle(sketch, "E333", {"center": v(217.5, 150.35) * mm, "radius": 2.5 * mm});
            skCircle(sketch, "E334", {"center": v(162.5, 150.35) * mm, "radius": 2.5 * mm});
            skCircle(sketch, "E335", {"center": v(76.25, 158.35) * mm, "radius": 1.5 * mm});
            skCircle(sketch, "E336", {"center": v(76.25, 145.35) * mm, "radius": 1.5 * mm});
            skLineSegment(sketch, "E337", {"start": v(-74, 157.35) * mm, "end": v(-40, 157.35) * mm});
            skLineSegment(sketch, "E338", {"start": v(-40, 157.35) * mm, "end": v(-40, 143.35) * mm});
            skLineSegment(sketch, "E339", {"start": v(-40, 143.35) * mm, "end": v(-74, 143.35) * mm});
            skLineSegment(sketch, "E340", {"start": v(-74, 143.35) * mm, "end": v(-74, 157.35) * mm});
            skCircle(sketch, "E341", {"center": v(-29.5, 150.35) * mm, "radius": 2.5 * mm});
            skCircle(sketch, "E342", {"center": v(-84.5, 150.35) * mm, "radius": 2.5 * mm});
            skCircle(sketch, "E343", {"center": v(-167.5, 147.35) * mm, "radius": 6.5 * mm});
            skCircle(sketch, "E344", {"center": v(-168.5, -6.15) * mm, "radius": 6.5 * mm});
            skCircle(sketch, "E345", {"center": v(-168.5, -35.65) * mm, "radius": 6.5 * mm});
            skCircle(sketch, "E346", {"center": v(-150.5, -5.15) * mm, "radius": 2 * mm});
            skCircle(sketch, "E347", {"center": v(-190, -5.65) * mm, "radius": 2 * mm});
            skCircle(sketch, "E348", {"center": v(-167.5, 116.85) * mm, "radius": 2.5 * mm});
            skCircle(sketch, "E349", {"center": v(-167, 86.85) * mm, "radius": 1 * mm});
            skCircle(sketch, "E350", {"center": v(-167, 53.85) * mm, "radius": 1 * mm});
            skCircle(sketch, "E351", {"center": v(-215.5, 116.85) * mm, "radius": 2 * mm});
            skSolve(sketch);
        }
        {
            var Q0;
            Q0=makeQuery(id+"F0.imprint","IMPRINT",FACE,{"disambiguationData":[TD([[makeQuery(id+"F0.imprint","IMPRINT",EDGE,{"derivedFrom":sQuery(id+"F0.wireOp",EDGE,"f901c926-723c-4426-8b4e-e114096da5cc")}),1.0]])]});
            var Q1;
            Q1=makeQuery(id+"F0.imprint","IMPRINT",FACE,{"disambiguationData":[TD([[makeQuery(id+"F0.imprint","IMPRINT",EDGE,{"derivedFrom":sQuery(id+"F0.wireOp",EDGE,"E0")}),1.0]])]});
            extrude(context, id + "F1", {"entities" : qUnion([Q0, Q1]), "oppositeDirection" : true, "depth" : 5 * mm, "offsetDistance" : 25 * mm});
        }
    });
